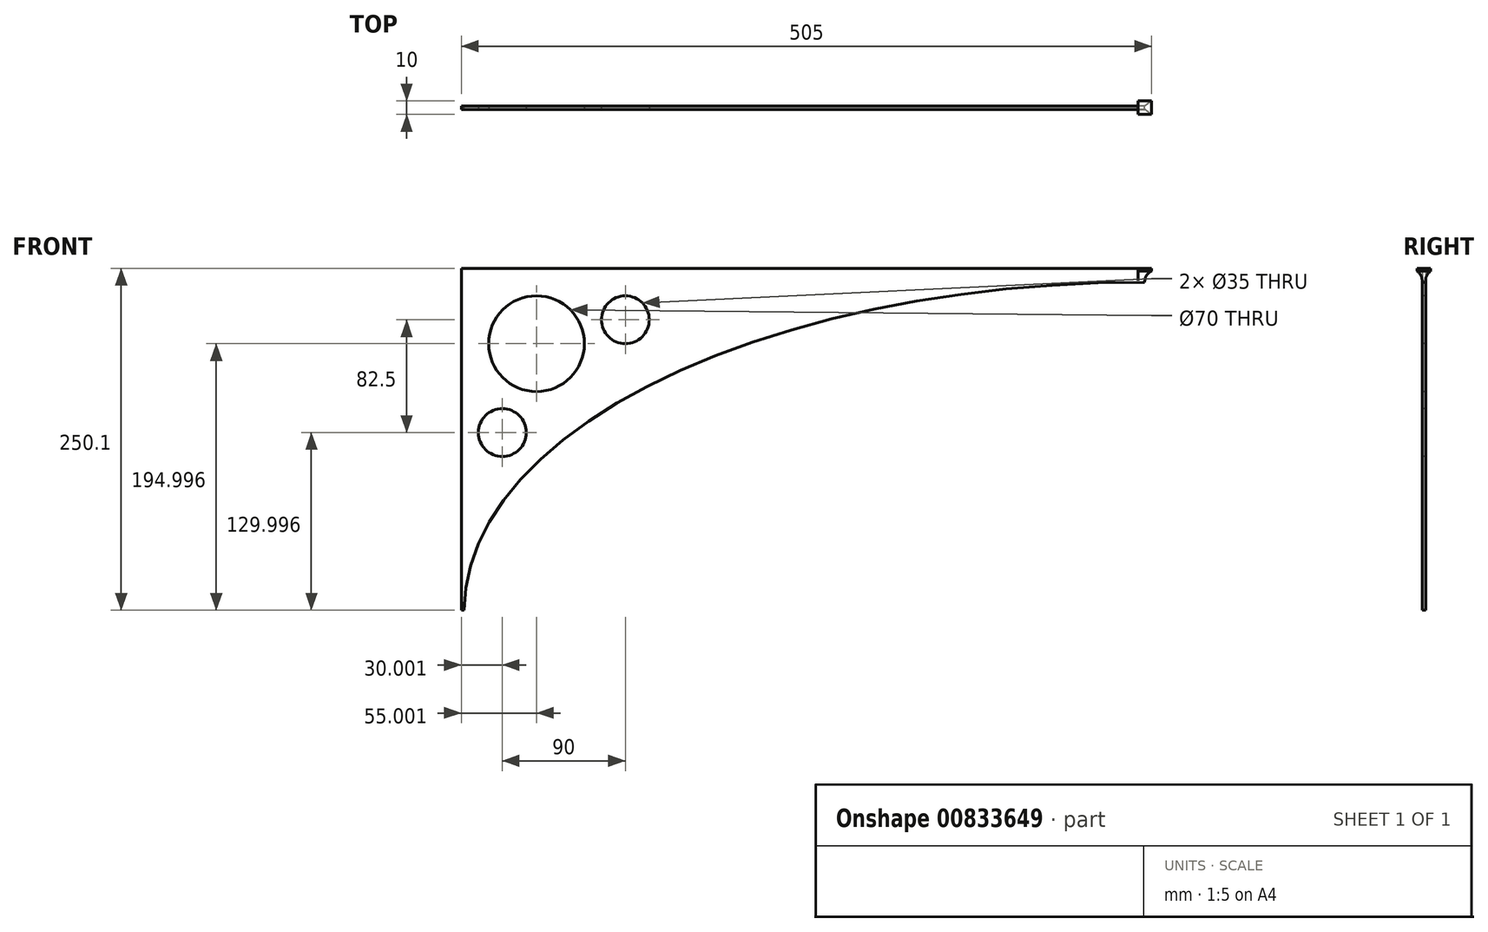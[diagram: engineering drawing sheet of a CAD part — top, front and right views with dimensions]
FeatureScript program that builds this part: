
annotation { "Feature Type Name" : "Feature", "Feature Type Description" : "" }
export const myFeature = defineFeature(function(context is Context, id is Id, definition is map)
    precondition{}
    {
        {
            var Q0;
            Q0=qCreatedBy(makeId("Front.planeOp"),FACE);
            var sketch = newSketch(context, id + "F0", { "sketchPlane" : qUnion([Q0])});
            skLineSegment(sketch, "E0", {"start": v(-265.69, 164.73) * mm, "end": v(234.31, 164.73) * mm});
            skLineSegment(sketch, "E1", {"start": v(234.31, 164.73) * mm, "end": v(234.31, 154.73) * mm});
            skLineSegment(sketch, "E2", {"start": v(-265.69, 164.73) * mm, "end": v(-265.69, -85.27) * mm});
            skLineSegment(sketch, "E3", {"start": v(-265.69, -85.27) * mm, "end": v(-263.69, -85.27) * mm});
            skEllipticalArc(sketch, "E4", {});
            const initialGuessF0  = {"E4": [0.2343109268695116, -0.08527348190546036, -1, 0, 0.498, 0.24, 4.71238898038469, 0]};
            skSetInitialGuess(sketch, initialGuessF0);
            skSolve(sketch);
        }
        {
            var Q0;
            Q0=makeQuery(id+"F0.imprint","IMPRINT",FACE,{"disambiguationData":[TD([[makeQuery(id+"F0.imprint","IMPRINT",EDGE,{"derivedFrom":sQuery(id+"F0.wireOp",EDGE,"E0")}),-1.0]])]});
            extrude(context, id + "F1", {"entities" : qUnion([Q0]), "depth" : 2.5 * mm, "offsetDistance" : 25 * mm});
        }
        {
            var Q0;
            Q0=makeQuery(id+"F1.opExtrude","CAP_FACE",FACE,{"disambiguationData":[OSD([sQuery(id+"F0.wireOp",EDGE,"E0"),sQuery(id+"F0.wireOp",EDGE,"E1"),sQuery(id+"F0.wireOp",EDGE,"E2"),sQuery(id+"F0.wireOp",EDGE,"E3"),sQuery(id+"F0.wireOp",EDGE,"E4")])],"isStart":false});
            var sketch = newSketch(context, id + "F2", { "sketchPlane" : qUnion([Q0])});
            skCircle(sketch, "E5", {"center": v(-210.69, 109.73) * mm, "radius": 35 * mm});
            skCircle(sketch, "E6", {"center": v(-145.69, 127.23) * mm, "radius": 17.5 * mm});
            skLineSegment(sketch, "E7", {"start": v(-210.69, 109.73) * mm, "end": v(-210.69, 164.73) * mm});
            skCircle(sketch, "E8", {"center": v(-235.69, 44.73) * mm, "radius": 17.5 * mm});
            skLineSegment(sketch, "E9", {"start": v(-210.69, 109.73) * mm, "end": v(-265.69, 109.73) * mm});
            skSolve(sketch);
        }
        {
            var Q0;
            Q0=sQuery(id+"F2.wireOp",VERTEX,"E5.center");
            var Q1;
            Q1=makeQuery(id+"F1.opExtrude","SWEPT_BODY",BODY,{"disambiguationData":[OSD([sQuery(id+"F0.wireOp",EDGE,"E0"),sQuery(id+"F0.wireOp",EDGE,"E1"),sQuery(id+"F0.wireOp",EDGE,"E2"),sQuery(id+"F0.wireOp",EDGE,"E3"),sQuery(id+"F0.wireOp",EDGE,"E4")])]});
            hole(context, id + "F3", {"style" : HoleStyle.SIMPLE, "endStyle" : HoleEndStyle.THROUGH, "holeDiameter" : 70 * mm, "majorDiameter" : 5 * mm, "isTappedThrough" : true, "tappedDepth" : 12 * mm, "tapClearance" : 3, "locations" : qUnion([Q0]), "scope" : qUnion([Q1])});
        }
        {
            var Q0;
            Q0=sQuery(id+"F2.wireOp",VERTEX,"E6.center");
            var Q1;
            Q1=sQuery(id+"F2.wireOp",VERTEX,"E8.center");
            var Q2;
            Q2=makeQuery(id+"F1.opExtrude","SWEPT_BODY",BODY,{"disambiguationData":[OSD([sQuery(id+"F0.wireOp",EDGE,"E0"),sQuery(id+"F0.wireOp",EDGE,"E1"),sQuery(id+"F0.wireOp",EDGE,"E2"),sQuery(id+"F0.wireOp",EDGE,"E3"),sQuery(id+"F0.wireOp",EDGE,"E4")])]});
            hole(context, id + "F4", {"style" : HoleStyle.SIMPLE, "endStyle" : HoleEndStyle.THROUGH, "holeDiameter" : 35 * mm, "majorDiameter" : 5 * mm, "isTappedThrough" : true, "tappedDepth" : 12 * mm, "tapClearance" : 3, "locations" : qUnion([Q0, Q1]), "scope" : qUnion([Q2])});
        }
        {
            var Q0;
            Q0=makeQuery(id+"F1.opExtrude","SWEPT_FACE",FACE,{"disambiguationData":[OSD([sQuery(id+"F0.wireOp",EDGE,"E0")])]});
            var sketch = newSketch(context, id + "F5", { "sketchPlane" : qUnion([Q0])});
            skLineSegment(sketch, "E10.bottom", {"start": v(239.31, 3.75) * mm, "end": v(229.31, 3.75) * mm});
            skLineSegment(sketch, "E10.top", {"start": v(239.31, -6.25) * mm, "end": v(229.31, -6.25) * mm});
            skLineSegment(sketch, "E10.left", {"start": v(239.31, 3.75) * mm, "end": v(239.31, -6.25) * mm});
            skLineSegment(sketch, "E10.right", {"start": v(229.31, 3.75) * mm, "end": v(229.31, -6.25) * mm});
            skPoint(sketch, "E10.middle", {"position": v(234.31, -1.25) * mm});
            skLineSegment(sketch, "E11", {"start": v(234.31, 0) * mm, "end": v(229.31, 0) * mm});
            skLineSegment(sketch, "E12", {"start": v(234.31, 0) * mm, "end": v(234.31, -2.5) * mm});
            skLineSegment(sketch, "E13", {"start": v(234.31, -2.5) * mm, "end": v(229.31, -2.5) * mm});
            skLineSegment(sketch, "E14", {"start": v(229.31, -2.5) * mm, "end": v(229.31, -6.25) * mm});
            skSolve(sketch);
        }
        {
            var Q0;
            {var subQ1=sQuery(id+"F5.wireOp",EDGE,"E10.bottom");Q0=makeQuery(id+"F5.imprint","IMPRINT",FACE,{"disambiguationData":[TD([[makeQuery(id+"F5.imprint","IMPRINT",EDGE,{"derivedFrom":subQ1}),1.0]])]});}
            var Q1;
            {var subQ3=sQuery(id+"F5.wireOp",EDGE,"E11");Q1=makeQuery(id+"F5.imprint","IMPRINT",FACE,{"disambiguationData":[TD([[makeQuery(id+"F5.imprint","IMPRINT",EDGE,{"derivedFrom":subQ3}),-1.0]])]});}
            extrude(context, id + "F6", {"entities" : qUnion([Q0, Q1]), "operationType" : NewBodyOperationType.ADD, "oppositeDirection" : true, "depth" : 2 * mm, "offsetDistance" : 25 * mm});
        }
        {
            var Q0;
            {var subQ1=sQuery(id+"F5.wireOp",EDGE,"E10.bottom");Q0=makeQuery(id+"F5.imprint","IMPRINT",FACE,{"disambiguationData":[TD([[makeQuery(id+"F5.imprint","IMPRINT",EDGE,{"derivedFrom":subQ1}),1.0]])]});}
            var Q1;
            {var subQ3=sQuery(id+"F5.wireOp",EDGE,"E11");Q1=makeQuery(id+"F5.imprint","IMPRINT",FACE,{"disambiguationData":[TD([[makeQuery(id+"F5.imprint","IMPRINT",EDGE,{"derivedFrom":subQ3}),-1.0]])]});}
            extrude(context, id + "F7", {"entities" : qUnion([Q0, Q1]), "operationType" : NewBodyOperationType.ADD, "depth" : 0.1 * mm, "offsetDistance" : 25 * mm});
        }
        {
            var Q0;
            Q0=makeQuery(id+"F6.boolean.opBoolean","INTERSECT",EDGE,{"derivedFrom":[makeQuery(id+"F1.opExtrude","SWEPT_FACE",FACE,{"disambiguationData":[OSD([sQuery(id+"F0.wireOp",EDGE,"E1")])]}),makeQuery(id+"F6.opExtrude","CAP_FACE",FACE,{"disambiguationData":[OSD([sQuery(id+"F5.wireOp",EDGE,"E10.bottom"),sQuery(id+"F5.wireOp",EDGE,"E10.top"),sQuery(id+"F5.wireOp",EDGE,"E10.left"),sQuery(id+"F5.wireOp",EDGE,"E10.right"),sQuery(id+"F5.wireOp",EDGE,"E14")])],"isStart":false})]});
            var Q1;
            Q1=makeQuery(id+"F6.boolean.opBoolean","INTERSECT",EDGE,{"derivedFrom":[makeQuery(id+"F1.opExtrude","CAP_FACE",FACE,{"disambiguationData":[OSD([sQuery(id+"F0.wireOp",EDGE,"E0"),sQuery(id+"F0.wireOp",EDGE,"E1"),sQuery(id+"F0.wireOp",EDGE,"E2"),sQuery(id+"F0.wireOp",EDGE,"E3"),sQuery(id+"F0.wireOp",EDGE,"E4")])],"isStart":false}),makeQuery(id+"F6.opExtrude","CAP_FACE",FACE,{"disambiguationData":[OSD([sQuery(id+"F5.wireOp",EDGE,"E10.bottom"),sQuery(id+"F5.wireOp",EDGE,"E10.top"),sQuery(id+"F5.wireOp",EDGE,"E10.left"),sQuery(id+"F5.wireOp",EDGE,"E10.right"),sQuery(id+"F5.wireOp",EDGE,"E14")])],"isStart":false})]});
            var Q2;
            Q2=makeQuery(id+"F6.boolean.opBoolean","INTERSECT",EDGE,{"derivedFrom":[makeQuery(id+"F1.opExtrude","CAP_FACE",FACE,{"disambiguationData":[OSD([sQuery(id+"F0.wireOp",EDGE,"E0"),sQuery(id+"F0.wireOp",EDGE,"E1"),sQuery(id+"F0.wireOp",EDGE,"E2"),sQuery(id+"F0.wireOp",EDGE,"E3"),sQuery(id+"F0.wireOp",EDGE,"E4")])],"isStart":true}),makeQuery(id+"F6.opExtrude","CAP_FACE",FACE,{"disambiguationData":[OSD([sQuery(id+"F5.wireOp",EDGE,"E10.bottom"),sQuery(id+"F5.wireOp",EDGE,"E10.top"),sQuery(id+"F5.wireOp",EDGE,"E10.left"),sQuery(id+"F5.wireOp",EDGE,"E10.right"),sQuery(id+"F5.wireOp",EDGE,"E14")])],"isStart":false})]});
            fillet(context, id + "F8", {"entities" : qUnion([Q0, Q1, Q2]), "radius" : 8 * mm, "tangentPropagation" : true, "allowEdgeOverflow" : false});
        }
    });
